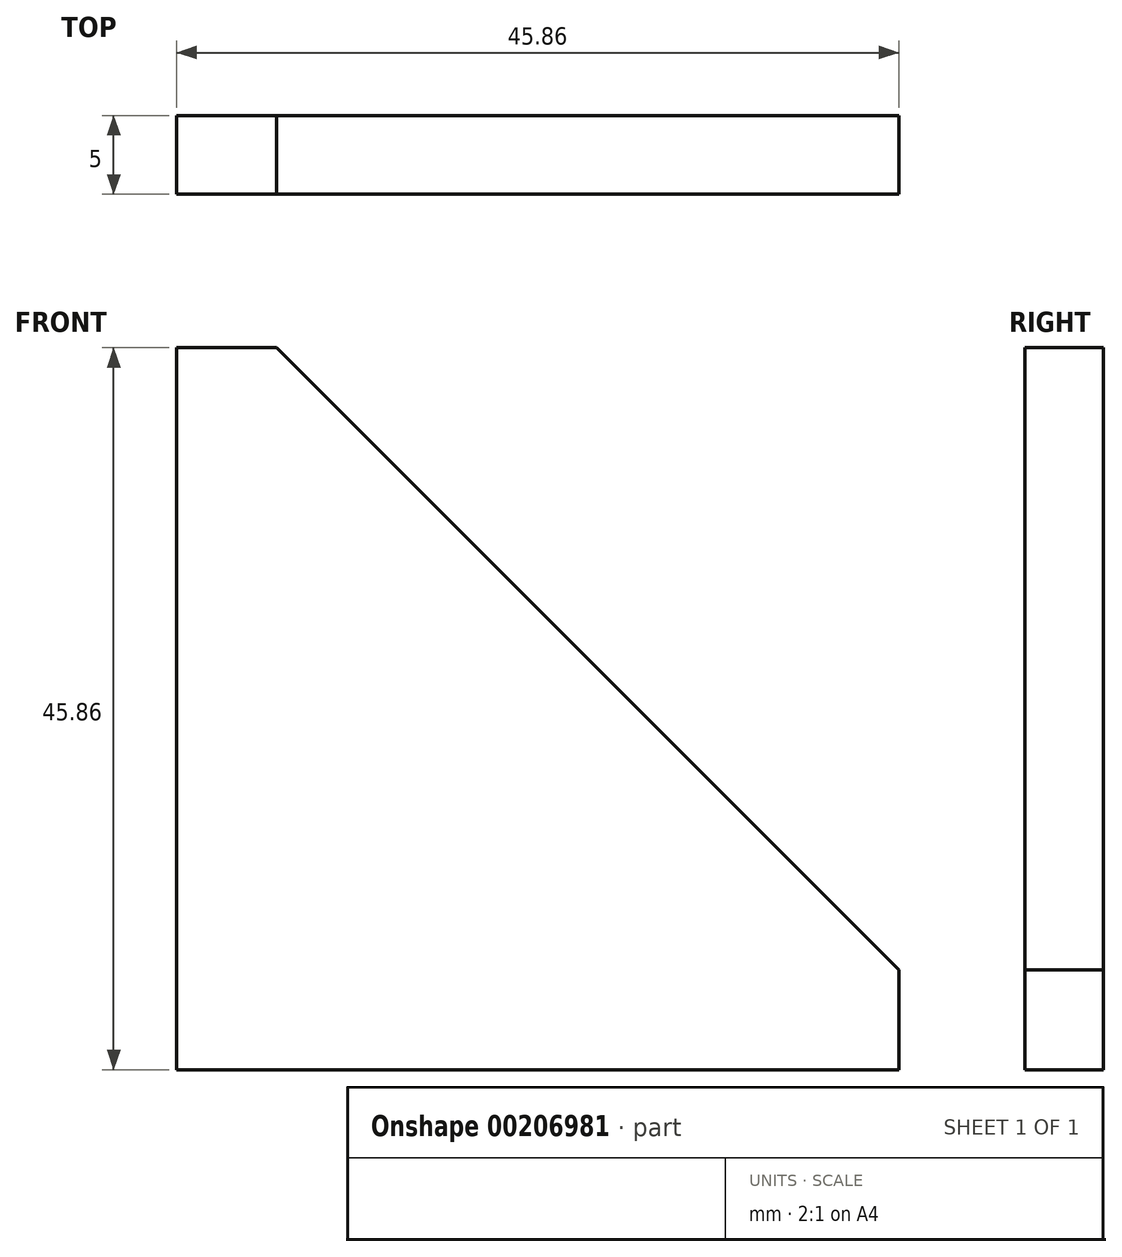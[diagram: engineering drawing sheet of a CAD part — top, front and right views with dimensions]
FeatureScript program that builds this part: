
annotation { "Feature Type Name" : "Feature", "Feature Type Description" : "" }
export const myFeature = defineFeature(function(context is Context, id is Id, definition is map)
    precondition{}
    {
        {
            assignVariable(context, id + "F0", {"name" : "screen_width", "anyValue" : 4});
        }
        {
            var Q0;
            Q0=qCreatedBy(makeId("Front.planeOp"),FACE);
            var sketch = newSketch(context, id + "F1", { "sketchPlane" : qUnion([Q0])});
            skLineSegment(sketch, "E0", {"start": v(-15.08, 29.86) * mm, "end": v(-15.08, -16) * mm});
            skLineSegment(sketch, "E1", {"start": v(-15.08, -16) * mm, "end": v(30.78, -16) * mm});
            skLineSegment(sketch, "E2", {"start": v(30.78, -16) * mm, "end": v(30.78, -9.65) * mm});
            skLineSegment(sketch, "E3", {"start": v(30.78, -9.65) * mm, "end": v(-8.73, 29.86) * mm});
            skLineSegment(sketch, "E4", {"start": v(-8.73, 29.86) * mm, "end": v(-15.08, 29.86) * mm});
            skSolve(sketch);
        }
        {
            var Q0;
            Q0=makeQuery(id+"F1.imprint","IMPRINT",FACE,{"disambiguationData":[TD([[makeQuery(id+"F1.imprint","IMPRINT",EDGE,{"derivedFrom":sQuery(id+"F1.wireOp",EDGE,"E0")}),1.0]])]});
            extrude(context, id + "F2", {"entities" : qUnion([Q0]), "depth" : (getVariable(context, 'screen_width') + 1) * mm});
        }
    });
